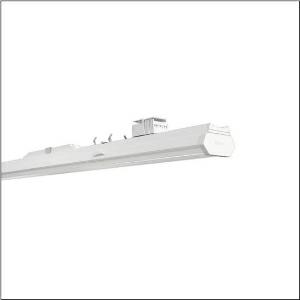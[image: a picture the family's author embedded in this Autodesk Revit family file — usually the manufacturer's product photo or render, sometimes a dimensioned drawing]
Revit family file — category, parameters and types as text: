
# Revit family: licross_r__11_protected_ho_51td12mn4f5m_c228
name_source: partatom
category: Lighting Fixtures
units: mm (PartAtom-declared; Revit-internal decimal feet)

## family parameters
Cut with Voids When Loaded = No
Host = Face
Light Source = No
Part Type = Normal
Room Calculation Point = No
Round Connector Dimension = Use Diameter
Shared = No

## types (1)
- --- (1 x LED, 15820 lm, 87.4 W, 4000K)
    Apparent Load = 87 VA
    CIE Flux Codes = 70 91 97 98 100
    Color Rendering = 80
    Color Temperature = 4000K
    Default Elevation = 1800 mm
    Description = Licross® 11 Protected HO, luminaire insert, of sheet steel, galvanised, coil coated, white, length: 1.500mm, width: 90mm, height: 101mm, LED rated luminous flux: 15.820lm, light colour: 840, control gear: ON/OFF Multilumen, with plug, 3-pole, with phase selection, mains connection: 220..240V, AC, 50/60Hz, rated input power: 87W, internal wiring halogen-free, primary light control with lens, of plastic, primary optical cover: cover, of PMMA, light emission: direct distribution, primary light characteristic: symmetric, protection rating (complete): IP54, insulation class (complete): insulation class I (protective earthing), certification: CE, ENEC, VDE, UKCA, protection symbol: D if used in an environment with non-conductive dust loads with corresponding accessories, impact resistance: IK06, permissible ambient temperature for indoor applications: -35..+35°C, corresponds to IFS (International Featured Standards) requirements for safety and quality in the food industry, reducing of maximum allowable ambient temperature of 5°C with ceiling mounting, LABS conformity tested according to VDMA 24364:2018-05, packaging unit: 1 piece
    Height = 92 mm
    Lamp = 1 x LED
    Lamp Light Flux = 15820 lm
    Lamp Power = 87.4 W
    Lamp count = 1
    Length = 1500 mm
    Luminous efficacy = 181 lm/W
    Manufacturer = Siteco
    ModVariant = No
    Model = 51TD12MN4F5M
    Mounting Place = Ceiling
    Mounting Type = Pendant
    Number of Poles = 1
    OnlyDefault = Yes
    Power Factor = 1
    Product Name = Licross® 11 Protected HO
    Product group = luminaire insert | ceiling pendant
    ProductGroupID = 902
    Protection Class = Protection class I
    Protection Degree = IP 54
    RLX_Detail_Level = 1
    RLX_Emergency_Light_Flux = 0 lm
    RLX_Emergency_Type = 0
    RLX_Emergency_Type_DB = No
    RlxData = <blob elided: 22061 chars, md5=ff43d387>
    Socket = socket
    Standby Power = 0 W
    System Light Flux = 15820 lm
    System Power = 87 W
    Type Comments = factory setting: luminous flux: 100 % | (A | C | E) | 203 mA
    Type Image = l_1256145.jpg
    URL = http://relux.com
    VarID = @adj_107505
    Voltage = 0 V
    Weight = 0.00 kg
    Width = 88 mm

## geometry (parser evidence)
native form markers: Blend x4, Sweep x11
no freeform markers — native parametric forms only
